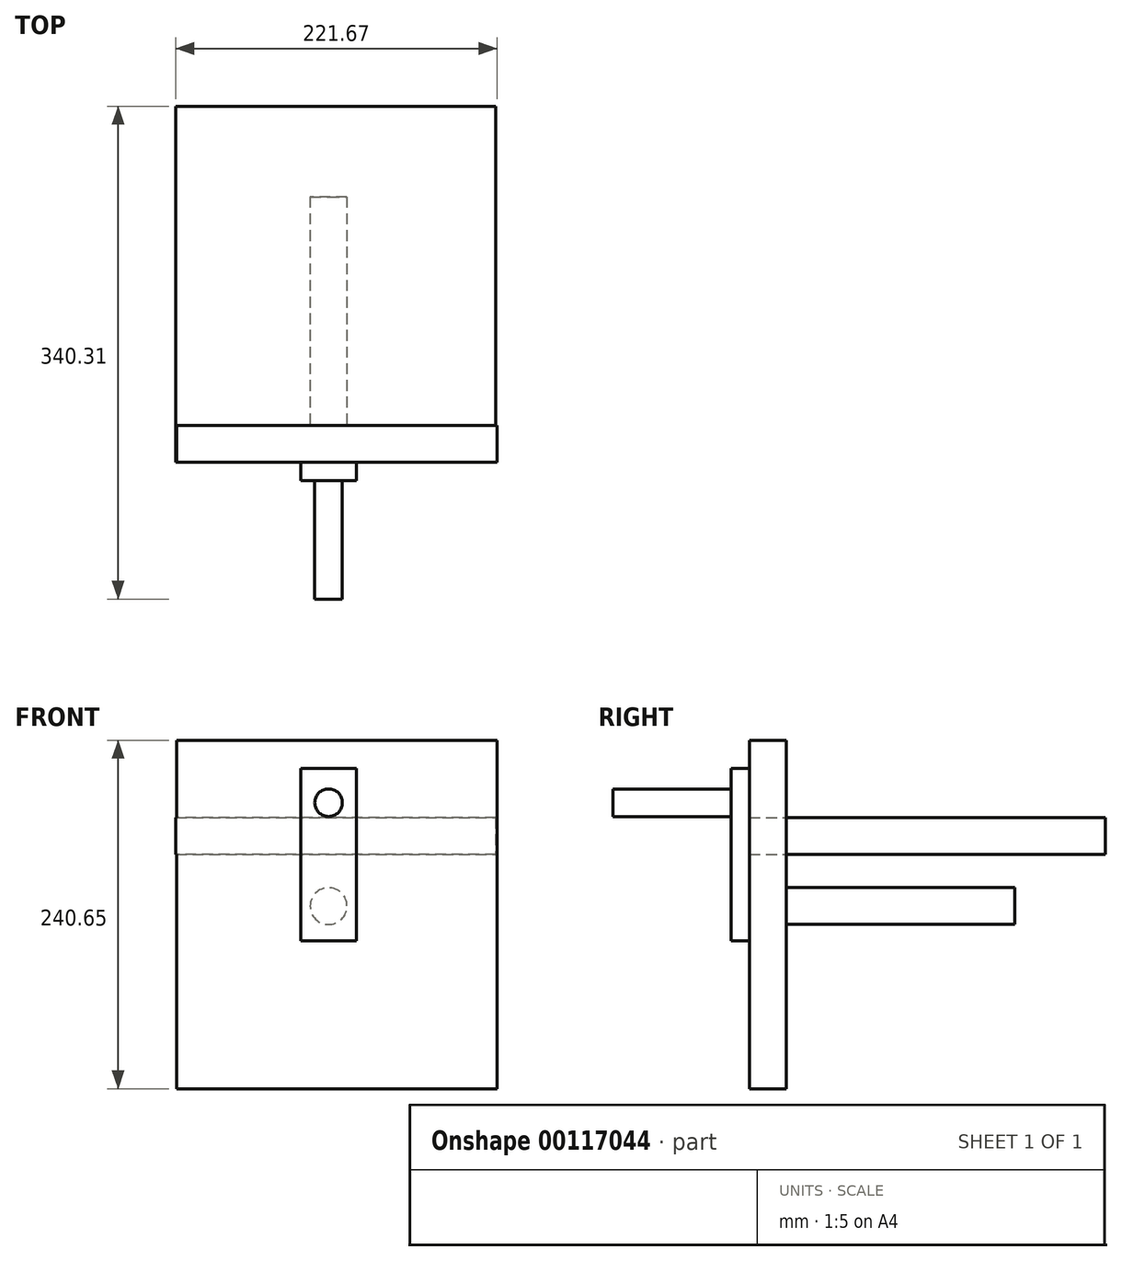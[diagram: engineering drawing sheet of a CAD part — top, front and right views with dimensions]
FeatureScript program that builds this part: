
annotation { "Feature Type Name" : "Feature", "Feature Type Description" : "" }
export const myFeature = defineFeature(function(context is Context, id is Id, definition is map)
    precondition{}
    {
        {
            var Q0;
            Q0=qCreatedBy(makeId("Front.planeOp"),FACE);
            var sketch = newSketch(context, id + "F0", { "sketchPlane" : qUnion([Q0])});
            skLineSegment(sketch, "E0.bottom", {"start": v(-19.33, 59.52) * mm, "end": v(19.33, 59.52) * mm});
            skLineSegment(sketch, "E0.top", {"start": v(-19.33, -59.52) * mm, "end": v(19.33, -59.52) * mm});
            skLineSegment(sketch, "E0.left", {"start": v(-19.33, 59.52) * mm, "end": v(-19.33, -59.52) * mm});
            skLineSegment(sketch, "E0.right", {"start": v(19.33, 59.52) * mm, "end": v(19.33, -59.52) * mm});
            skPoint(sketch, "E0.middle", {"position": v(0, 0) * mm});
            skPoint(sketch, "E1", {"position": v(0, 35.9) * mm});
            skPoint(sketch, "E2", {"position": v(0, -35.9) * mm});
            skSolve(sketch);
        }
        {
            var Q0;
            Q0=makeQuery(id+"F0.imprint","IMPRINT",FACE,{"disambiguationData":[TD([[makeQuery(id+"F0.imprint","IMPRINT",EDGE,{"derivedFrom":sQuery(id+"F0.wireOp",EDGE,"E0.bottom")}),-1.0]])]});
            extrude(context, id + "F1", {"entities" : qUnion([Q0]), "depth" : 12.7 * mm});
        }
        {
            var Q0;
            Q0=qCreatedBy(makeId("Front.planeOp"),FACE);
            var sketch = newSketch(context, id + "F2", { "sketchPlane" : qUnion([Q0])});
            skCircle(sketch, "E3", {"center": v(0, 35.78) * mm, "radius": 9.53 * mm});
            skSolve(sketch);
        }
        {
            var Q0;
            Q0=qCreatedBy(makeId("Front.planeOp"),FACE);
            var sketch = newSketch(context, id + "F3", { "sketchPlane" : qUnion([Q0])});
            skCircle(sketch, "E4", {"center": v(0, -35.64) * mm, "radius": 12.7 * mm});
            skSolve(sketch);
        }
        {
            var Q0;
            Q0 = qSketchRegion(id + "F3", true);
            extrude(context, id + "F4", {"entities" : qUnion([Q0]), "operationType" : NewBodyOperationType.ADD, "oppositeDirection" : true, "depth" : 183.45 * mm, "hasSecondDirection" : true, "secondDirectionOppositeDirection" : false, "secondDirectionDepth" : 8.28 * mm});
        }
        {
            var Q0;
            Q0 = qSketchRegion(id + "F2", true);
            extrude(context, id + "F5", {"entities" : qUnion([Q0]), "operationType" : NewBodyOperationType.ADD, "depth" : 94.33 * mm});
        }
        {
            var Q0;
            Q0=qCreatedBy(makeId("Front.planeOp"),FACE);
            var sketch = newSketch(context, id + "F6", { "sketchPlane" : qUnion([Q0])});
            skLineSegment(sketch, "E5.bottom", {"start": v(-104.76, 78.92) * mm, "end": v(116.27, 78.92) * mm});
            skLineSegment(sketch, "E5.top", {"start": v(-104.76, -161.73) * mm, "end": v(116.27, -161.73) * mm});
            skLineSegment(sketch, "E5.left", {"start": v(-104.76, 78.92) * mm, "end": v(-104.76, -161.73) * mm});
            skLineSegment(sketch, "E5.right", {"start": v(116.27, 78.92) * mm, "end": v(116.27, -161.73) * mm});
            skSolve(sketch);
        }
        {
            var Q0;
            Q0 = qSketchRegion(id + "F6", true);
            extrude(context, id + "F7", {"entities" : qUnion([Q0]), "operationType" : NewBodyOperationType.ADD, "oppositeDirection" : true, "depth" : 25.4 * mm});
        }
        {
            var Q0;
            Q0=qCreatedBy(makeId("Top.planeOp"),FACE);
            var sketch = newSketch(context, id + "F8", { "sketchPlane" : qUnion([Q0])});
            skLineSegment(sketch, "E6.bottom", {"start": v(-105.4, 245.98) * mm, "end": v(115.53, 245.98) * mm});
            skLineSegment(sketch, "E6.top", {"start": v(-105.4, 0) * mm, "end": v(115.53, 0) * mm});
            skLineSegment(sketch, "E6.left", {"start": v(-105.4, 0) * mm, "end": v(-105.4, 245.98) * mm});
            skLineSegment(sketch, "E6.right", {"start": v(115.53, 0) * mm, "end": v(115.53, 245.98) * mm});
            skSolve(sketch);
        }
        {
            var Q0;
            Q0=makeQuery(id+"F8.imprint","IMPRINT",FACE,{"disambiguationData":[TD([[makeQuery(id+"F8.imprint","IMPRINT",EDGE,{"derivedFrom":sQuery(id+"F8.wireOp",EDGE,"E6.bottom")}),-1.0]])]});
            extrude(context, id + "F9", {"entities" : qUnion([Q0]), "operationType" : NewBodyOperationType.ADD, "depth" : 25.4 * mm});
        }
    });
